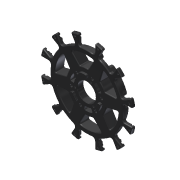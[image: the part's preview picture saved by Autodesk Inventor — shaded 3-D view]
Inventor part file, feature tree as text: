
AUTODESK INVENTOR PART (.ipt)
format: ipt  version: 2013 (Build 170138000, 138)  size: 1,251,328 bytes
history: native  units: in
note: dims shown in document units (in); Inventor stores cm internally (conversion verified against a paired STEP export)
features: chamfer x1, other x1, imported_body x1
ambient origin geometry x8: Origin, YZ Plane, XZ Plane, XY Plane, X Axis, Y Axis, Z Axis, Center Point
feature tree (3):
  chamfer  "Chamfer1"  [1 undecoded]
  other  "217-2585-003 Rev21"
  imported_body  "Base1"
note: 1 required parameter value undecoded (feature->parameter linkage not recoverable at this tier; creation-order binding heuristic only, values carry confidence <= 0.55)
